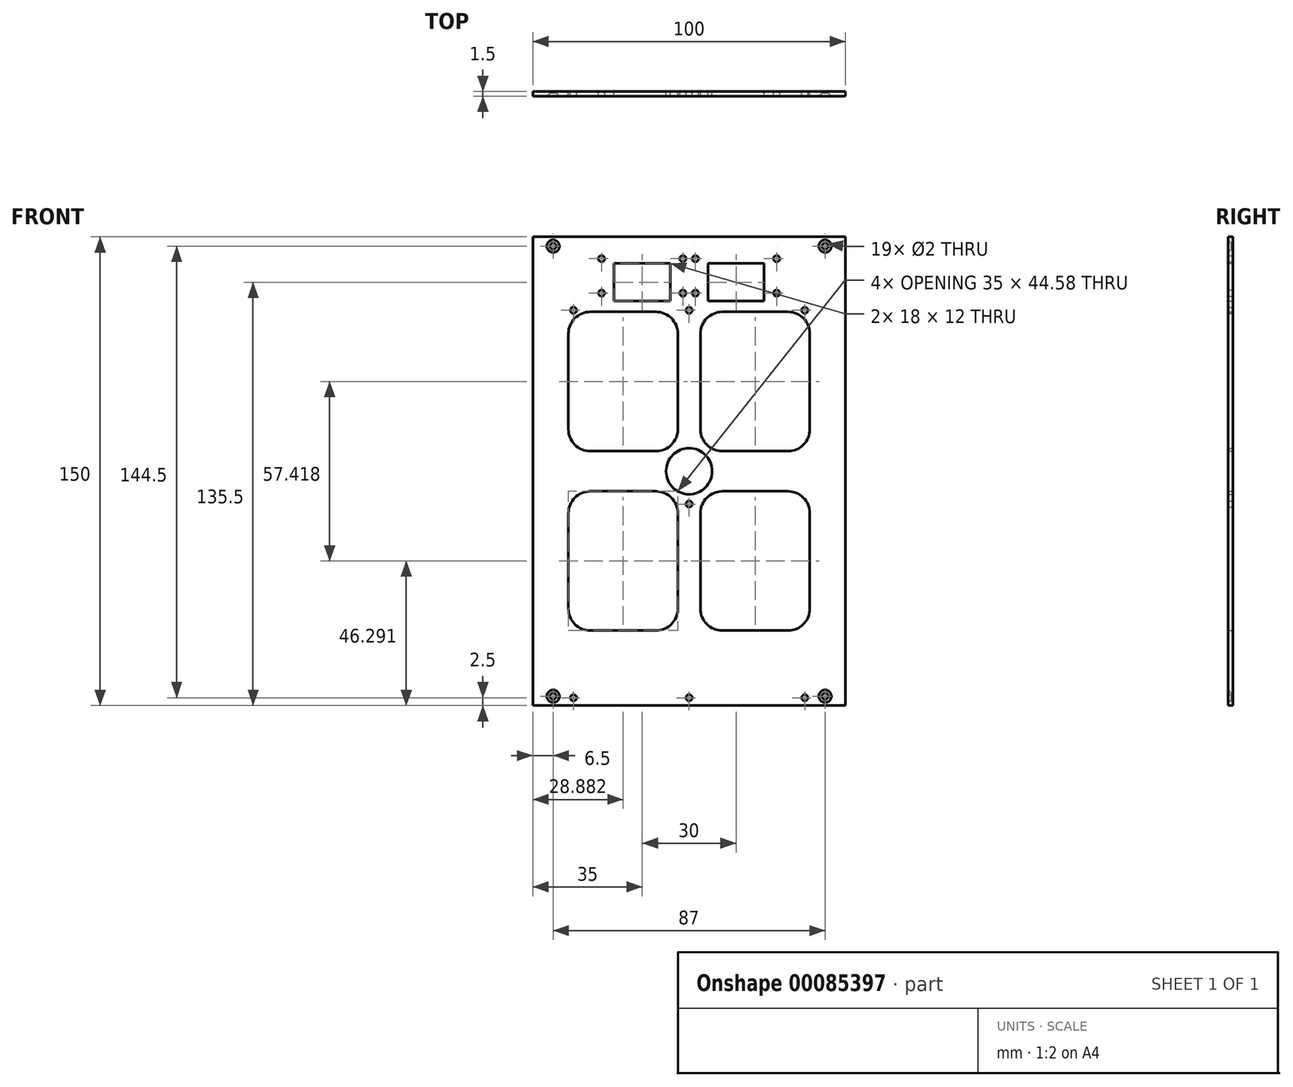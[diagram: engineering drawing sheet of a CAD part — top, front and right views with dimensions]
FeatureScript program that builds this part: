
annotation { "Feature Type Name" : "Feature", "Feature Type Description" : "" }
export const myFeature = defineFeature(function(context is Context, id is Id, definition is map)
    precondition{}
    {
        {
            var Q0;
            Q0=qCreatedBy(makeId("Front.planeOp"),FACE);
            var sketch = newSketch(context, id + "F0", { "sketchPlane" : qUnion([Q0])});
            skLineSegment(sketch, "E0.rect.bottom", {"start": v(-50, 75) * mm, "end": v(50, 75) * mm});
            skLineSegment(sketch, "E0.rect.top", {"start": v(-50, -75) * mm, "end": v(50, -75) * mm});
            skLineSegment(sketch, "E0.rect.left", {"start": v(-50, 75) * mm, "end": v(-50, -75) * mm});
            skLineSegment(sketch, "E0.rect.right", {"start": v(50, 75) * mm, "end": v(50, -75) * mm});
            skPoint(sketch, "E0.rect.middle", {"position": v(0, 0) * mm});
            skLineSegment(sketch, "E1.rect.bottom", {"start": v(-10.62, 6.42) * mm, "end": v(-31.62, 6.42) * mm});
            skLineSegment(sketch, "E1.rect.top", {"start": v(-10.62, 51) * mm, "end": v(-31.62, 51) * mm});
            skLineSegment(sketch, "E1.rect.left", {"start": v(-3.62, 13.42) * mm, "end": v(-3.62, 44) * mm});
            skLineSegment(sketch, "E1.rect.right", {"start": v(-38.62, 13.42) * mm, "end": v(-38.62, 44) * mm});
            skPoint(sketch, "E1.rect.middle", {"position": v(-21.12, 28.7) * mm});
            skPoint(sketch, "E2", {"position": v(0, 75) * mm});
            skPoint(sketch, "E3", {"position": v(-25, 75) * mm});
            skPoint(sketch, "E4.visualSharp", {"position": v(-3.62, 6.42) * mm});
            skArc(sketch, "E4.filletArc", {"start": v(-10.62, 6.42) * mm, "mid": v(-5.67, 8.47) * mm, "end": v(-3.62, 13.42) * mm});
            skPoint(sketch, "E5.visualSharp", {"position": v(-3.62, 51) * mm});
            skArc(sketch, "E5.filletArc", {"start": v(-3.62, 44) * mm, "mid": v(-5.67, 48.95) * mm, "end": v(-10.62, 51) * mm});
            skPoint(sketch, "E6.visualSharp", {"position": v(-38.62, 51) * mm});
            skArc(sketch, "E6.filletArc", {"start": v(-31.62, 51) * mm, "mid": v(-36.57, 48.95) * mm, "end": v(-38.62, 44) * mm});
            skPoint(sketch, "E7.visualSharp", {"position": v(-38.62, 6.42) * mm});
            skArc(sketch, "E7.filletArc", {"start": v(-38.62, 13.42) * mm, "mid": v(-36.57, 8.47) * mm, "end": v(-31.62, 6.42) * mm});
            skLineSegment(sketch, "E8.MirrorCS", {"start": v(3.62, 13.42) * mm, "end": v(3.62, 44) * mm});
            skArc(sketch, "E9.MirrorCS", {"start": v(3.62, 44) * mm, "mid": v(5.67, 48.95) * mm, "end": v(10.62, 51) * mm});
            skLineSegment(sketch, "E10.MirrorCS", {"start": v(10.62, 51) * mm, "end": v(31.62, 51) * mm});
            skPoint(sketch, "E11.MirrorP", {"position": v(38.62, 51) * mm});
            skArc(sketch, "E12.MirrorCS", {"start": v(31.62, 51) * mm, "mid": v(36.57, 48.95) * mm, "end": v(38.62, 44) * mm});
            skLineSegment(sketch, "E13.MirrorCS", {"start": v(38.62, 13.42) * mm, "end": v(38.62, 44) * mm});
            skPoint(sketch, "E14.MirrorP", {"position": v(38.62, 6.42) * mm});
            skLineSegment(sketch, "E15.MirrorCS", {"start": v(10.62, 6.42) * mm, "end": v(31.62, 6.42) * mm});
            skArc(sketch, "E16.MirrorCS", {"start": v(38.62, 13.42) * mm, "mid": v(36.57, 8.47) * mm, "end": v(31.62, 6.42) * mm});
            skPoint(sketch, "E17.MirrorP", {"position": v(3.62, 6.42) * mm});
            skArc(sketch, "E18.MirrorCS", {"start": v(10.62, 6.42) * mm, "mid": v(5.67, 8.47) * mm, "end": v(3.62, 13.42) * mm});
            skArc(sketch, "E19.MirrorCS", {"start": v(31.62, -51) * mm, "mid": v(36.57, -48.95) * mm, "end": v(38.62, -44) * mm});
            skArc(sketch, "E20.MirrorCS", {"start": v(38.62, -13.42) * mm, "mid": v(36.57, -8.47) * mm, "end": v(31.62, -6.42) * mm});
            skArc(sketch, "E21.MirrorCS", {"start": v(10.62, -6.42) * mm, "mid": v(5.67, -8.47) * mm, "end": v(3.62, -13.42) * mm});
            skArc(sketch, "E22.MirrorCS", {"start": v(3.62, -44) * mm, "mid": v(5.67, -48.95) * mm, "end": v(10.62, -51) * mm});
            skPoint(sketch, "E23.MirrorP", {"position": v(38.62, -51) * mm});
            skLineSegment(sketch, "E24.MirrorCS", {"start": v(38.62, -13.42) * mm, "end": v(38.62, -44) * mm});
            skPoint(sketch, "E25.MirrorP", {"position": v(38.62, -6.42) * mm});
            skLineSegment(sketch, "E26.MirrorCS", {"start": v(3.62, -13.42) * mm, "end": v(3.62, -44) * mm});
            skPoint(sketch, "E27.MirrorP", {"position": v(3.64, -53) * mm});
            skLineSegment(sketch, "E28.MirrorCS", {"start": v(10.62, -6.42) * mm, "end": v(31.62, -6.42) * mm});
            skLineSegment(sketch, "E29.MirrorCS", {"start": v(10.62, -51) * mm, "end": v(31.62, -51) * mm});
            skPoint(sketch, "E30.MirrorP", {"position": v(3.62, -6.42) * mm});
            skArc(sketch, "E31.MirrorCS", {"start": v(-10.62, -6.42) * mm, "mid": v(-5.67, -8.47) * mm, "end": v(-3.62, -13.42) * mm});
            skArc(sketch, "E32.MirrorCS", {"start": v(-3.62, -44) * mm, "mid": v(-5.67, -48.95) * mm, "end": v(-10.62, -51) * mm});
            skArc(sketch, "E33.MirrorCS", {"start": v(-38.62, -13.42) * mm, "mid": v(-36.57, -8.47) * mm, "end": v(-31.62, -6.42) * mm});
            skArc(sketch, "E34.MirrorCS", {"start": v(-31.62, -51) * mm, "mid": v(-36.57, -48.95) * mm, "end": v(-38.62, -44) * mm});
            skPoint(sketch, "E35.MirrorP", {"position": v(-21.12, -28.7) * mm});
            skPoint(sketch, "E36.MirrorP", {"position": v(-3.62, -6.42) * mm});
            skPoint(sketch, "E37.MirrorP", {"position": v(-38.62, -51) * mm});
            skLineSegment(sketch, "E38.MirrorCS", {"start": v(-10.62, -6.42) * mm, "end": v(-31.62, -6.42) * mm});
            skLineSegment(sketch, "E39.MirrorCS", {"start": v(-10.62, -51) * mm, "end": v(-31.62, -51) * mm});
            skPoint(sketch, "E40.MirrorP", {"position": v(-3.62, -51) * mm});
            skLineSegment(sketch, "E41.MirrorCS", {"start": v(-3.62, -13.42) * mm, "end": v(-3.62, -44) * mm});
            skLineSegment(sketch, "E42.MirrorCS", {"start": v(-38.62, -13.42) * mm, "end": v(-38.62, -44) * mm});
            skPoint(sketch, "E43.MirrorP", {"position": v(-38.62, -6.42) * mm});
            skCircle(sketch, "E44", {"center": v(0, 0) * mm, "radius": 7.37 * mm});
            skLineSegment(sketch, "E45.bottom", {"start": v(-24, 66.5) * mm, "end": v(-6, 66.5) * mm});
            skLineSegment(sketch, "E45.top", {"start": v(-24, 54.5) * mm, "end": v(-6, 54.5) * mm});
            skLineSegment(sketch, "E45.left", {"start": v(-24, 66.5) * mm, "end": v(-24, 54.5) * mm});
            skLineSegment(sketch, "E45.right", {"start": v(-6, 66.5) * mm, "end": v(-6, 54.5) * mm});
            skPoint(sketch, "E46", {"position": v(-28, 57) * mm});
            skPoint(sketch, "E47", {"position": v(-28, 68) * mm});
            skPoint(sketch, "E48", {"position": v(-15, 66.5) * mm});
            skPoint(sketch, "E49", {"position": v(-15, 54.5) * mm});
            skLineSegment(sketch, "E50", {"start": v(-15, 66.5) * mm, "end": v(-15, 54.5) * mm});
            skPoint(sketch, "E51.MirrorP", {"position": v(-2, 68) * mm});
            skPoint(sketch, "E52.MirrorP", {"position": v(-2, 57) * mm});
            skPoint(sketch, "E53.MirrorP", {"position": v(2, 68) * mm});
            skPoint(sketch, "E54.MirrorP", {"position": v(28, 57) * mm});
            skPoint(sketch, "E55.MirrorP", {"position": v(2, 57) * mm});
            skLineSegment(sketch, "E56.MirrorCS", {"start": v(6, 66.5) * mm, "end": v(6, 54.5) * mm});
            skLineSegment(sketch, "E57.MirrorCS", {"start": v(24, 66.5) * mm, "end": v(6, 66.5) * mm});
            skLineSegment(sketch, "E58.MirrorCS", {"start": v(24, 66.5) * mm, "end": v(24, 54.5) * mm});
            skLineSegment(sketch, "E59.MirrorCS", {"start": v(15, 66.5) * mm, "end": v(15, 54.5) * mm});
            skPoint(sketch, "E60.MirrorP", {"position": v(15, 66.5) * mm});
            skPoint(sketch, "E61.MirrorP", {"position": v(28, 68) * mm});
            skLineSegment(sketch, "E62.MirrorCS", {"start": v(24, 54.5) * mm, "end": v(6, 54.5) * mm});
            skPoint(sketch, "E63.MirrorP", {"position": v(3.62, 51) * mm});
            skPoint(sketch, "E64.MirrorP", {"position": v(15, 54.5) * mm});
            skPoint(sketch, "E65", {"position": v(0, -75) * mm});
            skSolve(sketch);
        }
        {
            var Q0;
            Q0=makeQuery(id+"F0.imprint","IMPRINT",FACE,{"disambiguationData":[TD([[makeQuery(id+"F0.imprint","IMPRINT",EDGE,{"derivedFrom":sQuery(id+"F0.wireOp",EDGE,"E0.rect.bottom")}),-1.0]])]});
            extrude(context, id + "F1", {"entities" : qUnion([Q0]), "depth" : 1.5 * mm});
        }
        {
            var Q0;
            Q0=makeQuery(id+"F1.opExtrude","CAP_FACE",FACE,{"disambiguationData":[OSD([sQuery(id+"F0.wireOp",EDGE,"E0.rect.bottom"),sQuery(id+"F0.wireOp",EDGE,"E0.rect.top"),sQuery(id+"F0.wireOp",EDGE,"E0.rect.left"),sQuery(id+"F0.wireOp",EDGE,"E0.rect.right"),sQuery(id+"F0.wireOp",EDGE,"E1.rect.bottom"),sQuery(id+"F0.wireOp",EDGE,"E1.rect.top"),sQuery(id+"F0.wireOp",EDGE,"E1.rect.left"),sQuery(id+"F0.wireOp",EDGE,"E1.rect.right"),sQuery(id+"F0.wireOp",EDGE,"E4.filletArc"),sQuery(id+"F0.wireOp",EDGE,"E5.filletArc"),sQuery(id+"F0.wireOp",EDGE,"E6.filletArc"),sQuery(id+"F0.wireOp",EDGE,"E7.filletArc"),sQuery(id+"F0.wireOp",EDGE,"E8.MirrorCS"),sQuery(id+"F0.wireOp",EDGE,"E9.MirrorCS"),sQuery(id+"F0.wireOp",EDGE,"E10.MirrorCS"),sQuery(id+"F0.wireOp",EDGE,"E12.MirrorCS"),sQuery(id+"F0.wireOp",EDGE,"E13.MirrorCS"),sQuery(id+"F0.wireOp",EDGE,"E15.MirrorCS"),sQuery(id+"F0.wireOp",EDGE,"E16.MirrorCS"),sQuery(id+"F0.wireOp",EDGE,"E18.MirrorCS"),sQuery(id+"F0.wireOp",EDGE,"E19.MirrorCS"),sQuery(id+"F0.wireOp",EDGE,"E20.MirrorCS"),sQuery(id+"F0.wireOp",EDGE,"E21.MirrorCS"),sQuery(id+"F0.wireOp",EDGE,"E22.MirrorCS"),sQuery(id+"F0.wireOp",EDGE,"E24.MirrorCS"),sQuery(id+"F0.wireOp",EDGE,"E26.MirrorCS"),sQuery(id+"F0.wireOp",EDGE,"E28.MirrorCS"),sQuery(id+"F0.wireOp",EDGE,"E29.MirrorCS"),sQuery(id+"F0.wireOp",EDGE,"E31.MirrorCS"),sQuery(id+"F0.wireOp",EDGE,"E32.MirrorCS"),sQuery(id+"F0.wireOp",EDGE,"E33.MirrorCS"),sQuery(id+"F0.wireOp",EDGE,"E34.MirrorCS"),sQuery(id+"F0.wireOp",EDGE,"E38.MirrorCS"),sQuery(id+"F0.wireOp",EDGE,"E39.MirrorCS"),sQuery(id+"F0.wireOp",EDGE,"E41.MirrorCS"),sQuery(id+"F0.wireOp",EDGE,"E42.MirrorCS"),sQuery(id+"F0.wireOp",EDGE,"deea28ce-c4f6-4fc3-8f0f-82602a925565.rect.bottom"),sQuery(id+"F0.wireOp",EDGE,"deea28ce-c4f6-4fc3-8f0f-82602a925565.rect.top"),sQuery(id+"F0.wireOp",EDGE,"deea28ce-c4f6-4fc3-8f0f-82602a925565.rect.left"),sQuery(id+"F0.wireOp",EDGE,"deea28ce-c4f6-4fc3-8f0f-82602a925565.rect.right"),sQuery(id+"F0.wireOp",EDGE,"92293470-82ba-44ad-9286-e8a1911384cd.filletArc"),sQuery(id+"F0.wireOp",EDGE,"f783d059-47c1-4597-a3b5-ce5ed20d1783.filletArc"),sQuery(id+"F0.wireOp",EDGE,"7d8a2005-66fb-4448-9a0b-17e6f11710ed.filletArc"),sQuery(id+"F0.wireOp",EDGE,"bd1f88c4-01d0-4c1f-b818-689555ed0d3d.filletArc"),sQuery(id+"F0.wireOp",EDGE,"3de75153-5ae1-45d4-89d9-6fcf70203f930.MirrorCS"),sQuery(id+"F0.wireOp",EDGE,"3de75153-5ae1-45d4-89d9-6fcf70203f931.MirrorCS"),sQuery(id+"F0.wireOp",EDGE,"3de75153-5ae1-45d4-89d9-6fcf70203f932.MirrorCS"),sQuery(id+"F0.wireOp",EDGE,"3de75153-5ae1-45d4-89d9-6fcf70203f933.MirrorCS"),sQuery(id+"F0.wireOp",EDGE,"3de75153-5ae1-45d4-89d9-6fcf70203f937.MirrorCS"),sQuery(id+"F0.wireOp",EDGE,"3de75153-5ae1-45d4-89d9-6fcf70203f939.MirrorCS"),sQuery(id+"F0.wireOp",EDGE,"3de75153-5ae1-45d4-89d9-6fcf70203f9311.MirrorCS"),sQuery(id+"F0.wireOp",EDGE,"3de75153-5ae1-45d4-89d9-6fcf70203f9312.MirrorCS")])],"isStart":false});
            var sketch = newSketch(context, id + "F2", { "sketchPlane" : qUnion([Q0])});
            skPoint(sketch, "E66", {"position": v(-43.5, -72) * mm});
            skPoint(sketch, "E67.MirrorP", {"position": v(43.5, -72) * mm});
            skPoint(sketch, "E68.MirrorP", {"position": v(-43.5, 72) * mm});
            skPoint(sketch, "E69.MirrorP", {"position": v(43.5, 72) * mm});
            skSolve(sketch);
        }
        {
            var Q0;
            Q0=sQuery(id+"F2.wireOp",VERTEX,"E66");
            var Q1;
            Q1=sQuery(id+"F2.wireOp",VERTEX,"E67.MirrorP");
            var Q2;
            Q2=sQuery(id+"F2.wireOp",VERTEX,"E69.MirrorP");
            var Q3;
            Q3=sQuery(id+"F2.wireOp",VERTEX,"E68.MirrorP");
            var Q4;
            Q4=sQuery(id+"F2.wireOp",VERTEX,"f692f96d-b3ef-4b25-bd05-95c4abe1053b");
            var Q5;
            Q5=sQuery(id+"F2.wireOp",VERTEX,"6fb1c37c-decf-44f5-8bba-7a2e60b1c09a");
            var Q6;
            Q6=sQuery(id+"F2.wireOp",VERTEX,"e5432b45-bd6c-42e0-96c4-d4a1cdefc3be");
            var Q7;
            Q7=sQuery(id+"F2.wireOp",VERTEX,"cf76a1ca-a373-4096-b586-4708a9325641");
            var Q8;
            Q8=sQuery(id+"F2.wireOp",VERTEX,"19e9ac87-c4db-4f84-8793-d0dcfe6b89480.MirrorP");
            var Q9;
            Q9=sQuery(id+"F2.wireOp",VERTEX,"cf40c92d-3cb4-4fd1-9011-2b1b11cf86800.MirrorP");
            var Q10;
            Q10=sQuery(id+"F2.wireOp",VERTEX,"dbe2afd2-cc13-4726-9d4e-a7426feb8f1a0.MirrorP");
            var Q11;
            Q11=sQuery(id+"F2.wireOp",VERTEX,"da7565b5-0760-4871-9ab9-0602c46f39720.MirrorP");
            var Q12;
            Q12=sQuery(id+"F2.wireOp",VERTEX,"17fecccd-3962-452f-9978-7328e825eee30.MirrorP");
            var Q13;
            Q13=sQuery(id+"F2.wireOp",VERTEX,"4bd07c42-14cb-4c0a-9484-79320a5c3db60.MirrorP");
            var Q14;
            Q14=sQuery(id+"F2.wireOp",VERTEX,"4bebc43e-6cee-4dba-a944-25e79cf908630.MirrorP");
            var Q15;
            Q15=sQuery(id+"F2.wireOp",VERTEX,"e56d2771-9223-44ee-8796-3a5c91e851be0.MirrorP");
            var Q16;
            Q16=sQuery(id+"F2.wireOp",VERTEX,"fc323023-5ca8-47af-bc60-2d4e8e6fe2a30.MirrorP");
            var Q17;
            Q17=sQuery(id+"F2.wireOp",VERTEX,"0839c29d-2d7f-409f-b01c-e3268e62f07b0.MirrorP");
            var Q18;
            Q18=sQuery(id+"F2.wireOp",VERTEX,"a23aa490-2248-47f4-872f-093390e742580.MirrorP");
            var Q19;
            Q19=sQuery(id+"F2.wireOp",VERTEX,"f29489ae-a8f8-488d-b8ee-71de4e1048c30.MirrorP");
            var Q20;
            Q20=makeQuery(id+"F1.opExtrude","SWEPT_BODY",BODY,{"disambiguationData":[OSD([sQuery(id+"F0.wireOp",EDGE,"E0.rect.bottom"),sQuery(id+"F0.wireOp",EDGE,"E0.rect.top"),sQuery(id+"F0.wireOp",EDGE,"E0.rect.left"),sQuery(id+"F0.wireOp",EDGE,"E0.rect.right"),sQuery(id+"F0.wireOp",EDGE,"E1.rect.bottom"),sQuery(id+"F0.wireOp",EDGE,"E1.rect.top"),sQuery(id+"F0.wireOp",EDGE,"E1.rect.left"),sQuery(id+"F0.wireOp",EDGE,"E1.rect.right"),sQuery(id+"F0.wireOp",EDGE,"E4.filletArc"),sQuery(id+"F0.wireOp",EDGE,"E5.filletArc"),sQuery(id+"F0.wireOp",EDGE,"E6.filletArc"),sQuery(id+"F0.wireOp",EDGE,"E7.filletArc"),sQuery(id+"F0.wireOp",EDGE,"E8.MirrorCS"),sQuery(id+"F0.wireOp",EDGE,"E9.MirrorCS"),sQuery(id+"F0.wireOp",EDGE,"E10.MirrorCS"),sQuery(id+"F0.wireOp",EDGE,"E12.MirrorCS"),sQuery(id+"F0.wireOp",EDGE,"E13.MirrorCS"),sQuery(id+"F0.wireOp",EDGE,"E15.MirrorCS"),sQuery(id+"F0.wireOp",EDGE,"E16.MirrorCS"),sQuery(id+"F0.wireOp",EDGE,"E18.MirrorCS"),sQuery(id+"F0.wireOp",EDGE,"E19.MirrorCS"),sQuery(id+"F0.wireOp",EDGE,"E20.MirrorCS"),sQuery(id+"F0.wireOp",EDGE,"E21.MirrorCS"),sQuery(id+"F0.wireOp",EDGE,"E22.MirrorCS"),sQuery(id+"F0.wireOp",EDGE,"E24.MirrorCS"),sQuery(id+"F0.wireOp",EDGE,"E26.MirrorCS"),sQuery(id+"F0.wireOp",EDGE,"E28.MirrorCS"),sQuery(id+"F0.wireOp",EDGE,"E29.MirrorCS"),sQuery(id+"F0.wireOp",EDGE,"E31.MirrorCS"),sQuery(id+"F0.wireOp",EDGE,"E32.MirrorCS"),sQuery(id+"F0.wireOp",EDGE,"E33.MirrorCS"),sQuery(id+"F0.wireOp",EDGE,"E34.MirrorCS"),sQuery(id+"F0.wireOp",EDGE,"E38.MirrorCS"),sQuery(id+"F0.wireOp",EDGE,"E39.MirrorCS"),sQuery(id+"F0.wireOp",EDGE,"E41.MirrorCS"),sQuery(id+"F0.wireOp",EDGE,"E42.MirrorCS"),sQuery(id+"F0.wireOp",EDGE,"deea28ce-c4f6-4fc3-8f0f-82602a925565.rect.bottom"),sQuery(id+"F0.wireOp",EDGE,"deea28ce-c4f6-4fc3-8f0f-82602a925565.rect.top"),sQuery(id+"F0.wireOp",EDGE,"deea28ce-c4f6-4fc3-8f0f-82602a925565.rect.left"),sQuery(id+"F0.wireOp",EDGE,"deea28ce-c4f6-4fc3-8f0f-82602a925565.rect.right"),sQuery(id+"F0.wireOp",EDGE,"92293470-82ba-44ad-9286-e8a1911384cd.filletArc"),sQuery(id+"F0.wireOp",EDGE,"f783d059-47c1-4597-a3b5-ce5ed20d1783.filletArc"),sQuery(id+"F0.wireOp",EDGE,"7d8a2005-66fb-4448-9a0b-17e6f11710ed.filletArc"),sQuery(id+"F0.wireOp",EDGE,"bd1f88c4-01d0-4c1f-b818-689555ed0d3d.filletArc"),sQuery(id+"F0.wireOp",EDGE,"3de75153-5ae1-45d4-89d9-6fcf70203f930.MirrorCS"),sQuery(id+"F0.wireOp",EDGE,"3de75153-5ae1-45d4-89d9-6fcf70203f931.MirrorCS"),sQuery(id+"F0.wireOp",EDGE,"3de75153-5ae1-45d4-89d9-6fcf70203f932.MirrorCS"),sQuery(id+"F0.wireOp",EDGE,"3de75153-5ae1-45d4-89d9-6fcf70203f933.MirrorCS"),sQuery(id+"F0.wireOp",EDGE,"3de75153-5ae1-45d4-89d9-6fcf70203f937.MirrorCS"),sQuery(id+"F0.wireOp",EDGE,"3de75153-5ae1-45d4-89d9-6fcf70203f939.MirrorCS"),sQuery(id+"F0.wireOp",EDGE,"3de75153-5ae1-45d4-89d9-6fcf70203f9311.MirrorCS"),sQuery(id+"F0.wireOp",EDGE,"3de75153-5ae1-45d4-89d9-6fcf70203f9312.MirrorCS")])]});
            hole(context, id + "F3", {"style" : HoleStyle.C_SINK, "holeDiameter" : 2 * mm, "cSinkDiameter" : 4 * mm, "endStyle" : HoleEndStyle.THROUGH, "locations" : qUnion([Q0, Q1, Q2, Q3, Q4, Q5, Q6, Q7, Q8, Q9, Q10, Q11, Q12, Q13, Q14, Q15, Q16, Q17, Q18, Q19]), "scope" : qUnion([Q20]), "cSinkAngle" : 90 * degree});
        }
        {
            var Q0;
            Q0=sQuery(id+"F0.wireOp",VERTEX,"E47");
            var Q1;
            Q1=sQuery(id+"F0.wireOp",VERTEX,"E46");
            var Q2;
            Q2=sQuery(id+"F0.wireOp",VERTEX,"E52.MirrorP");
            var Q3;
            Q3=sQuery(id+"F0.wireOp",VERTEX,"E51.MirrorP");
            var Q4;
            Q4=sQuery(id+"F0.wireOp",VERTEX,"E53.MirrorP");
            var Q5;
            Q5=sQuery(id+"F0.wireOp",VERTEX,"E55.MirrorP");
            var Q6;
            Q6=sQuery(id+"F0.wireOp",VERTEX,"E54.MirrorP");
            var Q7;
            Q7=sQuery(id+"F0.wireOp",VERTEX,"E61.MirrorP");
            var Q8;
            Q8=makeQuery(id+"F1.opExtrude","SWEPT_BODY",BODY,{"disambiguationData":[OSD([sQuery(id+"F0.wireOp",EDGE,"E0.rect.bottom"),sQuery(id+"F0.wireOp",EDGE,"E0.rect.top"),sQuery(id+"F0.wireOp",EDGE,"E0.rect.left"),sQuery(id+"F0.wireOp",EDGE,"E0.rect.right"),sQuery(id+"F0.wireOp",EDGE,"E1.rect.bottom"),sQuery(id+"F0.wireOp",EDGE,"E1.rect.top"),sQuery(id+"F0.wireOp",EDGE,"E1.rect.left"),sQuery(id+"F0.wireOp",EDGE,"E1.rect.right"),sQuery(id+"F0.wireOp",EDGE,"E4.filletArc"),sQuery(id+"F0.wireOp",EDGE,"E5.filletArc"),sQuery(id+"F0.wireOp",EDGE,"E6.filletArc"),sQuery(id+"F0.wireOp",EDGE,"E7.filletArc"),sQuery(id+"F0.wireOp",EDGE,"E8.MirrorCS"),sQuery(id+"F0.wireOp",EDGE,"E9.MirrorCS"),sQuery(id+"F0.wireOp",EDGE,"E10.MirrorCS"),sQuery(id+"F0.wireOp",EDGE,"E12.MirrorCS"),sQuery(id+"F0.wireOp",EDGE,"E13.MirrorCS"),sQuery(id+"F0.wireOp",EDGE,"E15.MirrorCS"),sQuery(id+"F0.wireOp",EDGE,"E16.MirrorCS"),sQuery(id+"F0.wireOp",EDGE,"E18.MirrorCS"),sQuery(id+"F0.wireOp",EDGE,"E19.MirrorCS"),sQuery(id+"F0.wireOp",EDGE,"E20.MirrorCS"),sQuery(id+"F0.wireOp",EDGE,"E21.MirrorCS"),sQuery(id+"F0.wireOp",EDGE,"E22.MirrorCS"),sQuery(id+"F0.wireOp",EDGE,"E24.MirrorCS"),sQuery(id+"F0.wireOp",EDGE,"E26.MirrorCS"),sQuery(id+"F0.wireOp",EDGE,"E28.MirrorCS"),sQuery(id+"F0.wireOp",EDGE,"E29.MirrorCS"),sQuery(id+"F0.wireOp",EDGE,"E31.MirrorCS"),sQuery(id+"F0.wireOp",EDGE,"E32.MirrorCS"),sQuery(id+"F0.wireOp",EDGE,"E33.MirrorCS"),sQuery(id+"F0.wireOp",EDGE,"E34.MirrorCS"),sQuery(id+"F0.wireOp",EDGE,"E38.MirrorCS"),sQuery(id+"F0.wireOp",EDGE,"E39.MirrorCS"),sQuery(id+"F0.wireOp",EDGE,"E41.MirrorCS"),sQuery(id+"F0.wireOp",EDGE,"E42.MirrorCS"),sQuery(id+"F0.wireOp",EDGE,"E44"),sQuery(id+"F0.wireOp",EDGE,"E45.bottom"),sQuery(id+"F0.wireOp",EDGE,"E45.top"),sQuery(id+"F0.wireOp",EDGE,"E45.left"),sQuery(id+"F0.wireOp",EDGE,"E45.right"),sQuery(id+"F0.wireOp",EDGE,"E56.MirrorCS"),sQuery(id+"F0.wireOp",EDGE,"E57.MirrorCS"),sQuery(id+"F0.wireOp",EDGE,"E58.MirrorCS"),sQuery(id+"F0.wireOp",EDGE,"E62.MirrorCS")])]});
            hole(context, id + "F4", {"style" : HoleStyle.SIMPLE, "endStyle" : HoleEndStyle.THROUGH, "oppositeDirection" : true, "holeDiameter" : 2 * mm, "locations" : qUnion([Q0, Q1, Q2, Q3, Q4, Q5, Q6, Q7]), "scope" : qUnion([Q8]), "isTappedThrough" : true});
        }
        {
            var Q0;
            Q0=qCreatedBy(makeId("Front.planeOp"),FACE);
            var sketch = newSketch(context, id + "F5", { "sketchPlane" : qUnion([Q0])});
            skCircle(sketch, "E70", {"center": v(-37, -72.5) * mm, "radius": 1 * mm});
            skCircle(sketch, "E71.0.1.0", {"center": v(-37, -10.5) * mm, "radius": 1 * mm});
            skCircle(sketch, "E71.0.2.0", {"center": v(-37, 51.5) * mm, "radius": 1 * mm});
            skCircle(sketch, "E71.1.0.0", {"center": v(0, -72.5) * mm, "radius": 1 * mm});
            skCircle(sketch, "E71.1.1.0", {"center": v(0, -10.5) * mm, "radius": 1 * mm});
            skCircle(sketch, "E71.1.2.0", {"center": v(0, 51.5) * mm, "radius": 1 * mm});
            skCircle(sketch, "E71.2.0.0", {"center": v(37, -72.5) * mm, "radius": 1 * mm});
            skCircle(sketch, "E71.2.1.0", {"center": v(37, -10.5) * mm, "radius": 1 * mm});
            skCircle(sketch, "E71.2.2.0", {"center": v(37, 51.5) * mm, "radius": 1 * mm});
            skLineSegment(sketch, "E71.direction1", {"start": v(-37, -72.5) * mm, "end": v(0, -72.5) * mm, "construction": true});
            skLineSegment(sketch, "E71.direction2", {"start": v(-37, -72.5) * mm, "end": v(-37, -10.5) * mm, "construction": true});
            skSolve(sketch);
        }
        {
            var Q0;
            Q0=sQuery(id+"F5.wireOp",VERTEX,"E71.direction1.start");
            var Q1;
            Q1=sQuery(id+"F5.wireOp",VERTEX,"E71.direction1.end");
            var Q2;
            Q2=sQuery(id+"F5.wireOp",VERTEX,"E71.2.0.0.center");
            var Q3;
            Q3=sQuery(id+"F5.wireOp",VERTEX,"E71.1.1.0.center");
            var Q4;
            Q4=sQuery(id+"F5.wireOp",VERTEX,"E71.1.2.0.center");
            var Q5;
            Q5=sQuery(id+"F5.wireOp",VERTEX,"E71.2.2.0.center");
            var Q6;
            Q6=sQuery(id+"F5.wireOp",VERTEX,"E71.0.2.0.center");
            var Q7;
            Q7=makeQuery(id+"F1.opExtrude","SWEPT_BODY",BODY,{"disambiguationData":[OSD([sQuery(id+"F0.wireOp",EDGE,"E0.rect.bottom"),sQuery(id+"F0.wireOp",EDGE,"E0.rect.top"),sQuery(id+"F0.wireOp",EDGE,"E0.rect.left"),sQuery(id+"F0.wireOp",EDGE,"E0.rect.right"),sQuery(id+"F0.wireOp",EDGE,"E1.rect.bottom"),sQuery(id+"F0.wireOp",EDGE,"E1.rect.top"),sQuery(id+"F0.wireOp",EDGE,"E1.rect.left"),sQuery(id+"F0.wireOp",EDGE,"E1.rect.right"),sQuery(id+"F0.wireOp",EDGE,"E4.filletArc"),sQuery(id+"F0.wireOp",EDGE,"E5.filletArc"),sQuery(id+"F0.wireOp",EDGE,"E6.filletArc"),sQuery(id+"F0.wireOp",EDGE,"E7.filletArc"),sQuery(id+"F0.wireOp",EDGE,"E8.MirrorCS"),sQuery(id+"F0.wireOp",EDGE,"E9.MirrorCS"),sQuery(id+"F0.wireOp",EDGE,"E10.MirrorCS"),sQuery(id+"F0.wireOp",EDGE,"E12.MirrorCS"),sQuery(id+"F0.wireOp",EDGE,"E13.MirrorCS"),sQuery(id+"F0.wireOp",EDGE,"E15.MirrorCS"),sQuery(id+"F0.wireOp",EDGE,"E16.MirrorCS"),sQuery(id+"F0.wireOp",EDGE,"E18.MirrorCS"),sQuery(id+"F0.wireOp",EDGE,"E19.MirrorCS"),sQuery(id+"F0.wireOp",EDGE,"E20.MirrorCS"),sQuery(id+"F0.wireOp",EDGE,"E21.MirrorCS"),sQuery(id+"F0.wireOp",EDGE,"E22.MirrorCS"),sQuery(id+"F0.wireOp",EDGE,"E24.MirrorCS"),sQuery(id+"F0.wireOp",EDGE,"E26.MirrorCS"),sQuery(id+"F0.wireOp",EDGE,"E28.MirrorCS"),sQuery(id+"F0.wireOp",EDGE,"E29.MirrorCS"),sQuery(id+"F0.wireOp",EDGE,"E31.MirrorCS"),sQuery(id+"F0.wireOp",EDGE,"E32.MirrorCS"),sQuery(id+"F0.wireOp",EDGE,"E33.MirrorCS"),sQuery(id+"F0.wireOp",EDGE,"E34.MirrorCS"),sQuery(id+"F0.wireOp",EDGE,"E38.MirrorCS"),sQuery(id+"F0.wireOp",EDGE,"E39.MirrorCS"),sQuery(id+"F0.wireOp",EDGE,"E41.MirrorCS"),sQuery(id+"F0.wireOp",EDGE,"E42.MirrorCS"),sQuery(id+"F0.wireOp",EDGE,"E44"),sQuery(id+"F0.wireOp",EDGE,"E45.bottom"),sQuery(id+"F0.wireOp",EDGE,"E45.top"),sQuery(id+"F0.wireOp",EDGE,"E45.left"),sQuery(id+"F0.wireOp",EDGE,"E45.right"),sQuery(id+"F0.wireOp",EDGE,"E56.MirrorCS"),sQuery(id+"F0.wireOp",EDGE,"E57.MirrorCS"),sQuery(id+"F0.wireOp",EDGE,"E58.MirrorCS"),sQuery(id+"F0.wireOp",EDGE,"E62.MirrorCS")])]});
            hole(context, id + "F6", {"style" : HoleStyle.SIMPLE, "endStyle" : HoleEndStyle.THROUGH, "oppositeDirection" : true, "holeDiameter" : 2 * mm, "locations" : qUnion([Q0, Q1, Q2, Q3, Q4, Q5, Q6]), "scope" : qUnion([Q7]), "isTappedThrough" : true});
        }
    });
